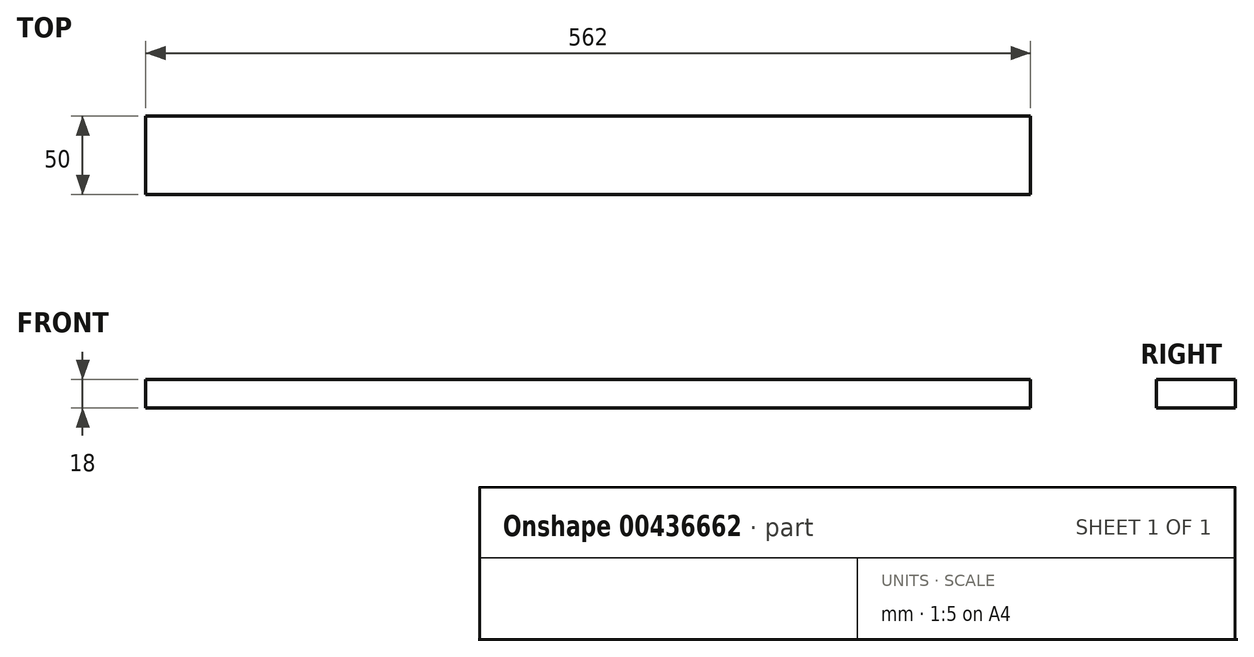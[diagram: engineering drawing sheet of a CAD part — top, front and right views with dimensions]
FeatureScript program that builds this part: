
annotation { "Feature Type Name" : "Feature", "Feature Type Description" : "" }
export const myFeature = defineFeature(function(context is Context, id is Id, definition is map)
    precondition{}
    {
        {
            var Q0;
            Q0=qCreatedBy(makeId("Right.planeOp"),FACE);
            var sketch = newSketch(context, id + "F0", { "sketchPlane" : qUnion([Q0])});
            skLineSegment(sketch, "E0.bottom", {"start": v(25, -9) * mm, "end": v(-25, -9) * mm});
            skLineSegment(sketch, "E0.top", {"start": v(25, 9) * mm, "end": v(-25, 9) * mm});
            skLineSegment(sketch, "E0.left", {"start": v(25, -9) * mm, "end": v(25, 9) * mm});
            skLineSegment(sketch, "E0.right", {"start": v(-25, -9) * mm, "end": v(-25, 9) * mm});
            skPoint(sketch, "E0.middle", {"position": v(0, 0) * mm});
            skSolve(sketch);
        }
        {
            var Q0;
            Q0=qSketchRegion(id+"F0",true);
            extrude(context, id + "F1", {"entities" : qUnion([Q0]), "depth" : 562 * mm});
        }
    });
